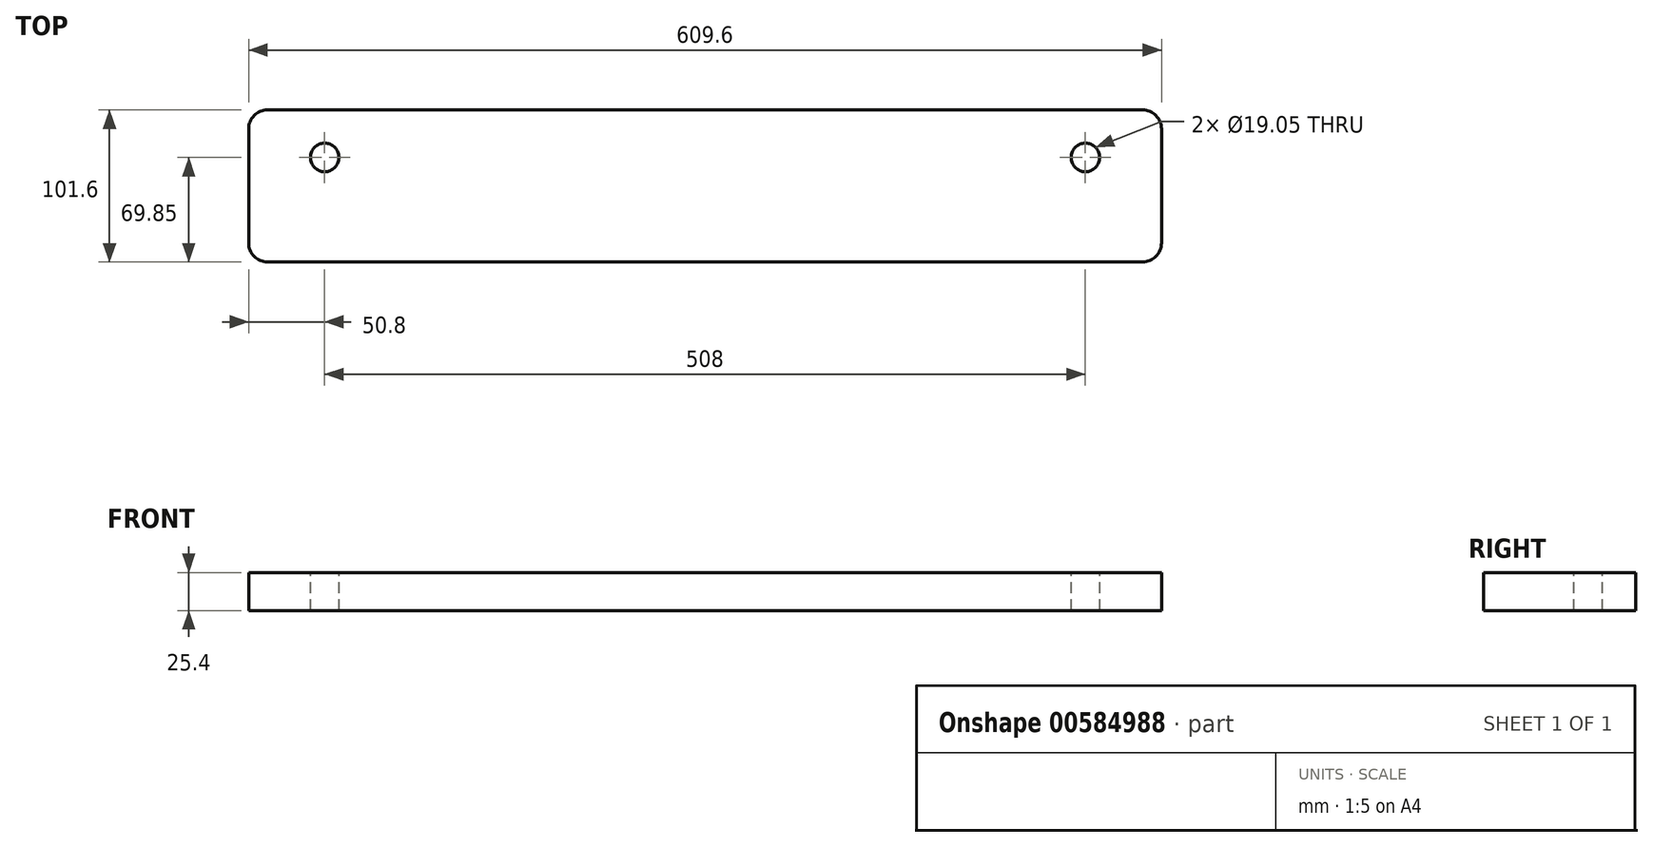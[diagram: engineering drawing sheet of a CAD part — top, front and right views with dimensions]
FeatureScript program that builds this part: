
annotation { "Feature Type Name" : "Feature", "Feature Type Description" : "" }
export const myFeature = defineFeature(function(context is Context, id is Id, definition is map)
    precondition{}
    {
        {
            var Q0;
            Q0=qCreatedBy(makeId("Top.planeOp"),FACE);
            var sketch = newSketch(context, id + "F0", { "sketchPlane" : qUnion([Q0])});
            skLineSegment(sketch, "E0.bottom", {"start": v(304.8, 50.8) * mm, "end": v(-304.8, 50.8) * mm});
            skLineSegment(sketch, "E0.top", {"start": v(304.8, -50.8) * mm, "end": v(-304.8, -50.8) * mm});
            skLineSegment(sketch, "E0.left", {"start": v(304.8, 50.8) * mm, "end": v(304.8, -50.8) * mm});
            skLineSegment(sketch, "E0.right", {"start": v(-304.8, 50.8) * mm, "end": v(-304.8, -50.8) * mm});
            skPoint(sketch, "E0.middle", {"position": v(0, 0) * mm});
            skSolve(sketch);
        }
        {
            var Q0;
            Q0 = qSketchRegion(id + "F0", true);
            extrude(context, id + "F1", {"entities" : qUnion([Q0]), "depth" : 25.4 * mm, "offsetDistance" : 25.4 * mm});
        }
        {
            var Q0;
            Q0=makeQuery(id+"F1.opExtrude","CAP_FACE",FACE,{"disambiguationData":[OSD([sQuery(id+"F0.wireOp",EDGE,"E0.bottom"),sQuery(id+"F0.wireOp",EDGE,"E0.top"),sQuery(id+"F0.wireOp",EDGE,"E0.left"),sQuery(id+"F0.wireOp",EDGE,"E0.right")])],"isStart":false});
            var sketch = newSketch(context, id + "F2", { "sketchPlane" : qUnion([Q0])});
            skPoint(sketch, "E1", {"position": v(-254, 19.05) * mm});
            skPoint(sketch, "E2.MirrorP", {"position": v(254, 19.05) * mm});
            skSolve(sketch);
        }
        {
            var Q0;
            Q0=sQuery(id+"F2.wireOp",VERTEX,"E1");
            var Q1;
            Q1=sQuery(id+"F2.wireOp",VERTEX,"E2.MirrorP");
            var Q2;
            Q2=makeQuery(id+"F1.opExtrude","SWEPT_BODY",BODY,{"disambiguationData":[OSD([sQuery(id+"F0.wireOp",EDGE,"E0.bottom"),sQuery(id+"F0.wireOp",EDGE,"E0.top"),sQuery(id+"F0.wireOp",EDGE,"E0.left"),sQuery(id+"F0.wireOp",EDGE,"E0.right")])]});
            hole(context, id + "F3", {"style" : HoleStyle.SIMPLE, "endStyle" : HoleEndStyle.THROUGH, "holeDiameter" : 19.05 * mm, "majorDiameter" : 6.35 * mm, "isTappedThrough" : true, "tappedDepth" : 12.7 * mm, "tapClearance" : 3, "locations" : qUnion([Q0, Q1]), "scope" : qUnion([Q2])});
        }
        {
            var Q0;
            Q0=makeQuery(id+"F1.opExtrude","SWEPT_EDGE",EDGE,{"disambiguationData":[OSD([sQuery(id+"F0.wireOp",EDGE,"E0.bottom"),sQuery(id+"F0.wireOp",EDGE,"E0.right")])]});
            var Q1;
            Q1=makeQuery(id+"F1.opExtrude","SWEPT_EDGE",EDGE,{"disambiguationData":[OSD([sQuery(id+"F0.wireOp",EDGE,"E0.top"),sQuery(id+"F0.wireOp",EDGE,"E0.right")])]});
            var Q2;
            Q2=makeQuery(id+"F1.opExtrude","SWEPT_EDGE",EDGE,{"disambiguationData":[OSD([sQuery(id+"F0.wireOp",EDGE,"E0.top"),sQuery(id+"F0.wireOp",EDGE,"E0.left")])]});
            var Q3;
            Q3=makeQuery(id+"F1.opExtrude","SWEPT_EDGE",EDGE,{"disambiguationData":[OSD([sQuery(id+"F0.wireOp",EDGE,"E0.bottom"),sQuery(id+"F0.wireOp",EDGE,"E0.left")])]});
            fillet(context, id + "F4", {"entities" : qUnion([Q0, Q1, Q2, Q3]), "radius" : 12.7 * mm, "tangentPropagation" : true, "allowEdgeOverflow" : false});
        }
    });
